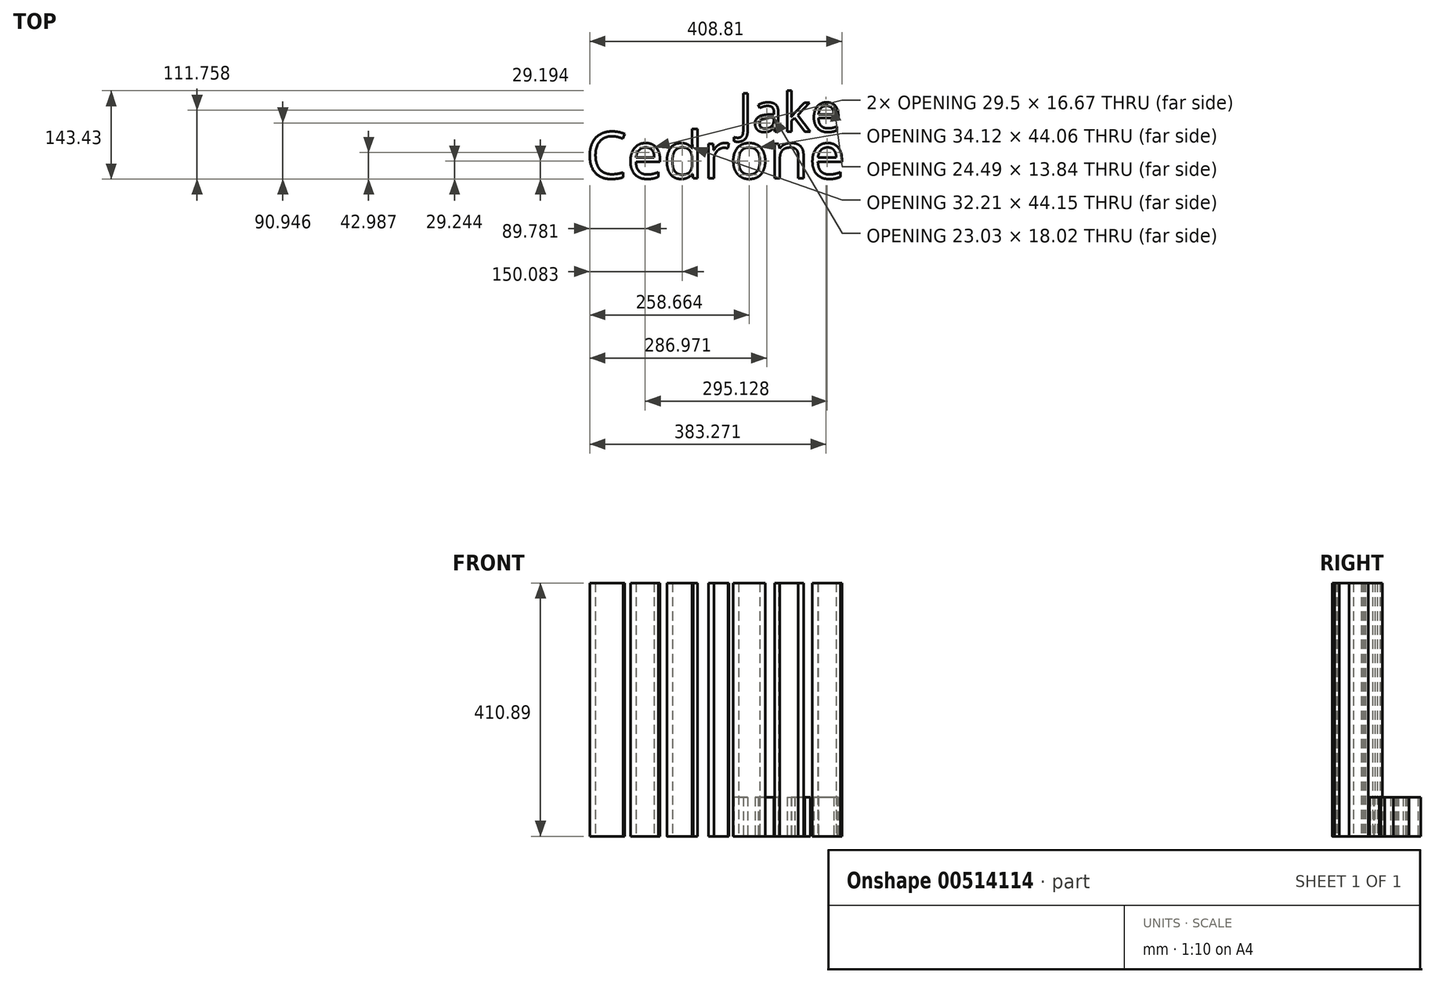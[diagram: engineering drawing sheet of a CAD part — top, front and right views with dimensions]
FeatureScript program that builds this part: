
annotation { "Feature Type Name" : "Feature", "Feature Type Description" : "" }
export const myFeature = defineFeature(function(context is Context, id is Id, definition is map)
    precondition{}
    {
        {
            var Q0;
            Q0=qCreatedBy(makeId("Top.planeOp"),FACE);
            var sketch = newSketch(context, id + "F0", { "sketchPlane" : qUnion([Q0])});
            skText(sketch, "E0", { "text": "Jake", "fontName": "OpenSans-Regular.ttf"});
            const initialGuessF0  = {"E0": [-0.175, 0, 1, 0, 0.06301]};
            skSetInitialGuess(sketch, initialGuessF0);
            skSolve(sketch);
        }
        {
            var Q0;
            Q0 = qSketchRegion(id + "F0", true);
            extrude(context, id + "F1", {"entities" : qUnion([Q0]), "depth" : 63.5 * mm});
        }
        {
            var Q0;
            Q0=qCreatedBy(makeId("Top.planeOp"),FACE);
            var sketch = newSketch(context, id + "F2", { "sketchPlane" : qUnion([Q0])});
            skText(sketch, "E1", { "text": "Cedrone", "fontName": "OpenSans-Regular.ttf"});
            const initialGuessF2  = {"E1": [-0.42207, -0.07589, 1, 0, 0.07589]};
            skSetInitialGuess(sketch, initialGuessF2);
            skSolve(sketch);
        }
        {
            var Q0;
            Q0 = qSketchRegion(id + "F2", true);
            extrude(context, id + "F3", {"entities" : qUnion([Q0]), "depth" : 410.9 * mm});
        }
    });
